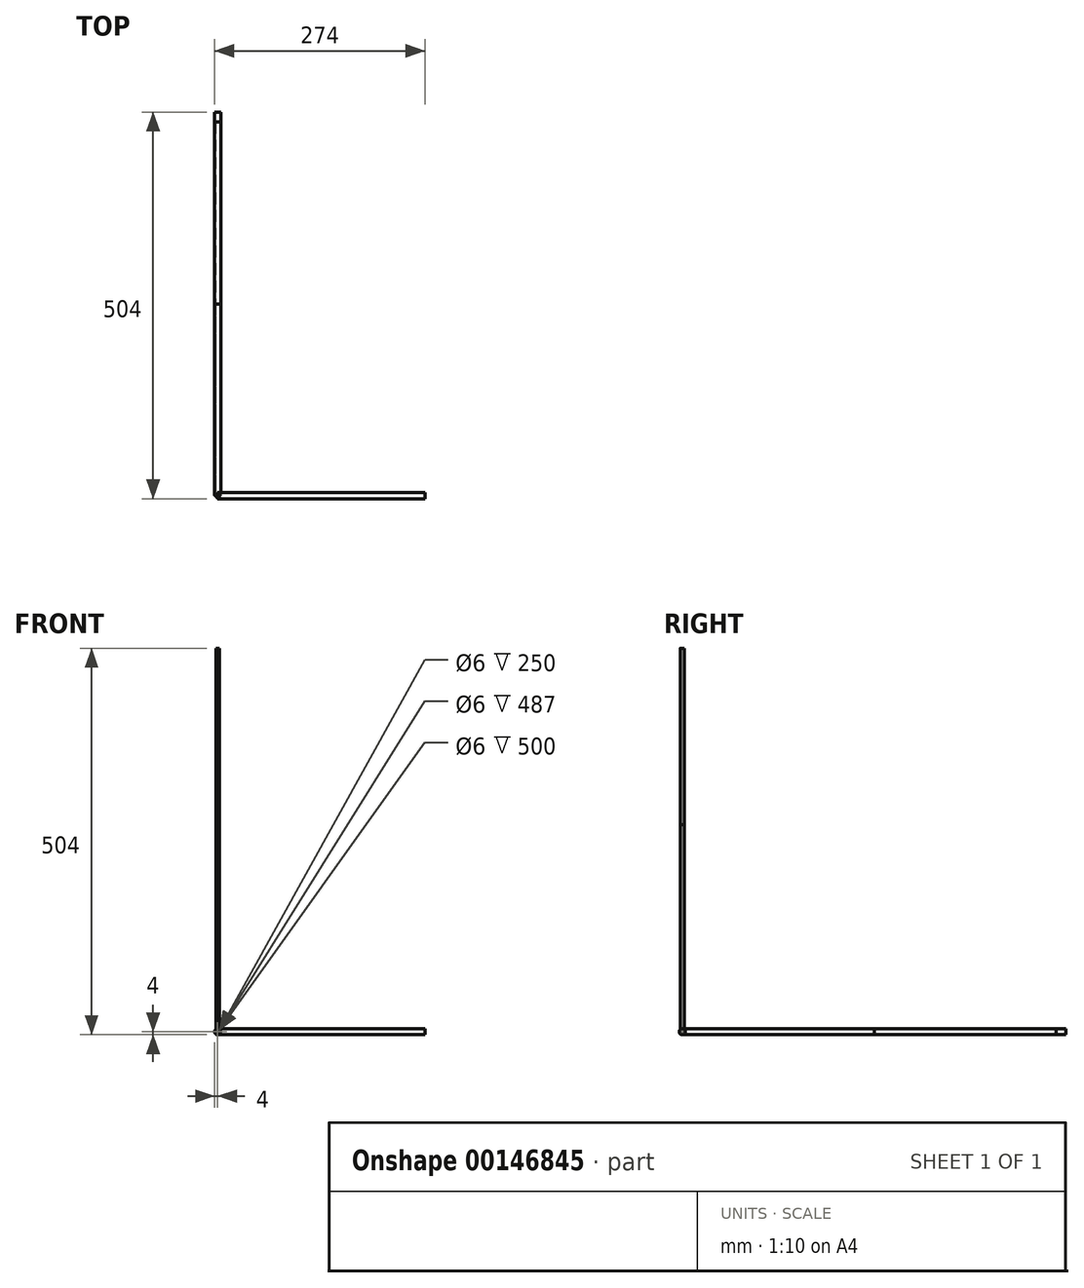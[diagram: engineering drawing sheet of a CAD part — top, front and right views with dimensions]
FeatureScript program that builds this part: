
annotation { "Feature Type Name" : "Feature", "Feature Type Description" : "" }
export const myFeature = defineFeature(function(context is Context, id is Id, definition is map)
    precondition{}
    {
        {
            var Q0;
            Q0=qCreatedBy(makeId("Front.planeOp"),FACE);
            var sketch = newSketch(context, id + "F0", { "sketchPlane" : qUnion([Q0])});
            skCircle(sketch, "E0", {"center": v(0, 0) * mm, "radius": 4 * mm});
            skCircle(sketch, "E1", {"center": v(0, 0) * mm, "radius": 3 * mm});
            skSolve(sketch);
        }
        {
            var Q0;
            Q0=qSketchRegion(id+"F0",true);
            extrude(context, id + "F1", {"entities" : qUnion([Q0]), "oppositeDirection" : true, "depth" : 500 * mm});
        }
        {
            var Q0;
            Q0=qSketchRegion(id+"F0",true);
            extrude(context, id + "F2", {"entities" : qUnion([Q0]), "oppositeDirection" : true, "depth" : 487 * mm});
        }
        {
            var Q0;
            Q0=qCreatedBy(makeId("Top.planeOp"),FACE);
            var sketch = newSketch(context, id + "F3", { "sketchPlane" : qUnion([Q0])});
            skCircle(sketch, "E2", {"center": v(0, 0) * mm, "radius": 2.5 * mm});
            skSolve(sketch);
        }
        {
            var Q0;
            Q0=qSketchRegion(id+"F3",true);
            extrude(context, id + "F4", {"entities" : qUnion([Q0]), "depth" : 500 * mm});
        }
        {
            var Q0;
            Q0=qSketchRegion(id+"F0",true);
            extrude(context, id + "F5", {"entities" : qUnion([Q0]), "oppositeDirection" : true, "depth" : 250 * mm});
        }
        {
            var Q0;
            Q0=qCreatedBy(makeId("Right.planeOp"),FACE);
            var sketch = newSketch(context, id + "F6", { "sketchPlane" : qUnion([Q0])});
            skCircle(sketch, "E3", {"center": v(0, 0) * mm, "radius": 4 * mm});
            skSolve(sketch);
        }
        {
            var Q0;
            Q0=qSketchRegion(id+"F6",true);
            extrude(context, id + "F7", {"entities" : qUnion([Q0]), "depth" : 270 * mm});
        }
        {
            var Q0;
            Q0=qSketchRegion(id+"F3",true);
            extrude(context, id + "F8", {"entities" : qUnion([Q0]), "depth" : 270 * mm});
        }
    });
